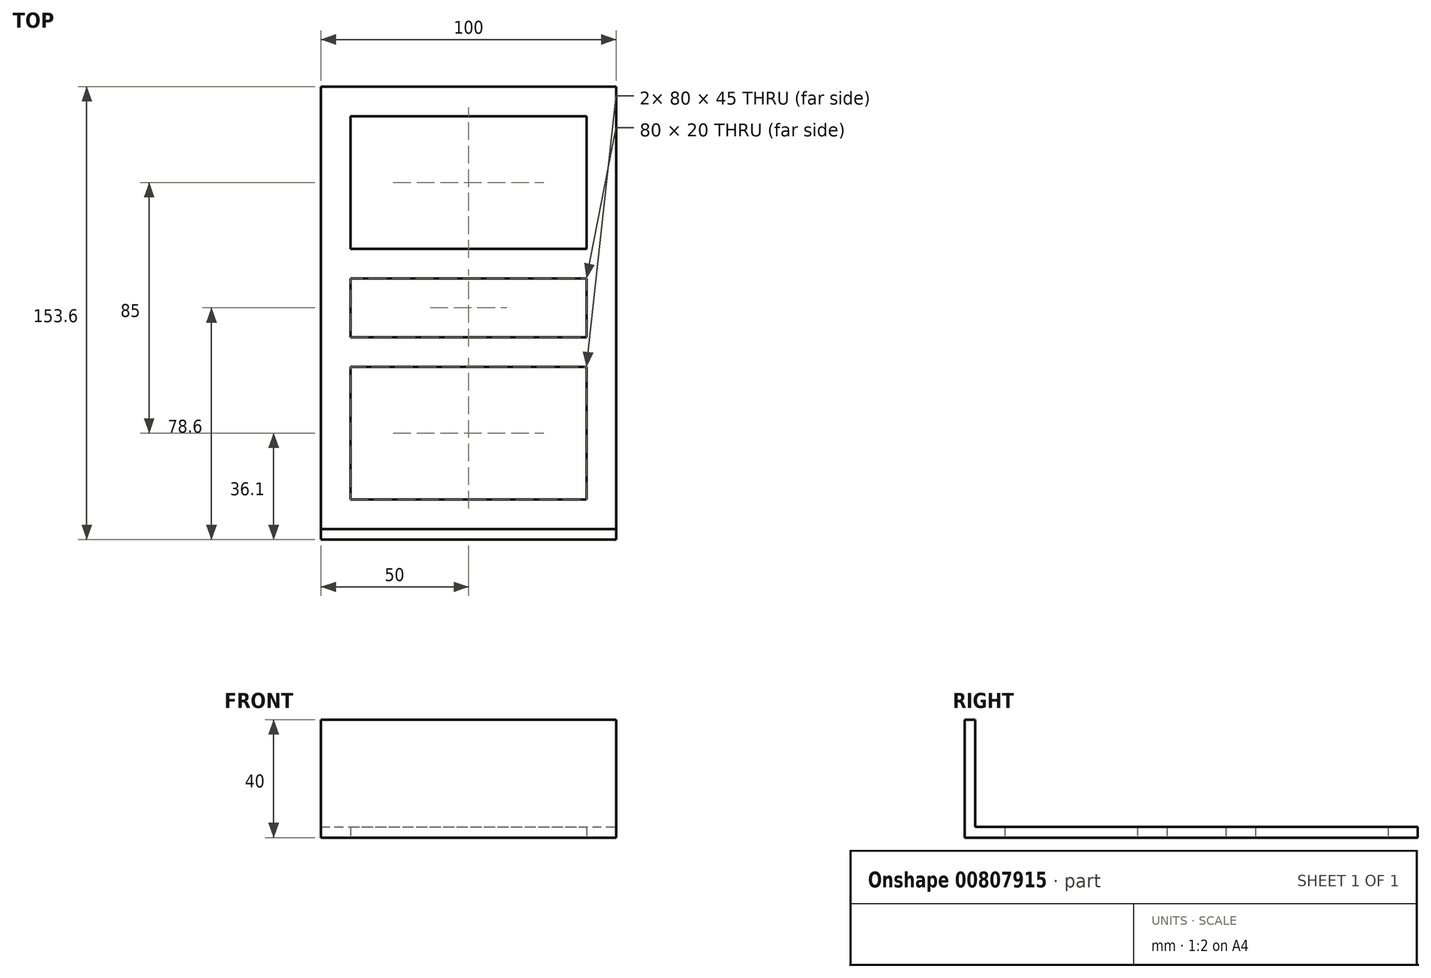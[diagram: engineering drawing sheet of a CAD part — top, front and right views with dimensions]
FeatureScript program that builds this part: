
annotation { "Feature Type Name" : "Feature", "Feature Type Description" : "" }
export const myFeature = defineFeature(function(context is Context, id is Id, definition is map)
    precondition{}
    {
        {
            var Q0;
            Q0=qCreatedBy(makeId("Top.planeOp"),FACE);
            var sketch = newSketch(context, id + "F0", { "sketchPlane" : qUnion([Q0])});
            skLineSegment(sketch, "E0.bottom", {"start": v(-50, 75) * mm, "end": v(50, 75) * mm});
            skLineSegment(sketch, "E0.top", {"start": v(-50, -75) * mm, "end": v(50, -75) * mm});
            skLineSegment(sketch, "E0.left", {"start": v(-50, 75) * mm, "end": v(-50, -75) * mm});
            skLineSegment(sketch, "E0.right", {"start": v(50, 75) * mm, "end": v(50, -75) * mm});
            skPoint(sketch, "E0.middle", {"position": v(0, 0) * mm});
            skLineSegment(sketch, "E1.bottom", {"start": v(-40, 65) * mm, "end": v(40, 65) * mm});
            skLineSegment(sketch, "E1.top", {"start": v(-40, -65) * mm, "end": v(40, -65) * mm});
            skLineSegment(sketch, "E1.left", {"start": v(-40, 65) * mm, "end": v(-40, -65) * mm});
            skLineSegment(sketch, "E1.right", {"start": v(40, 65) * mm, "end": v(40, -65) * mm});
            skLineSegment(sketch, "E2", {"start": v(-40, 20) * mm, "end": v(40, 20) * mm});
            skLineSegment(sketch, "E3", {"start": v(-40, -20) * mm, "end": v(40, -20) * mm});
            skLineSegment(sketch, "E4", {"start": v(-40, 10) * mm, "end": v(40, 10) * mm});
            skLineSegment(sketch, "E5", {"start": v(-40, -10) * mm, "end": v(40, -10) * mm});
            skSolve(sketch);
        }
        {
            var Q0;
            Q0=makeQuery(id+"F0.imprint","IMPRINT",FACE,{"disambiguationData":[TD([[makeQuery(id+"F0.imprint","IMPRINT",EDGE,{"derivedFrom":sQuery(id+"F0.wireOp",EDGE,"E0.bottom")}),-1.0]])]});
            var Q1;
            {var subQ0=sQuery(id+"F0.wireOp",EDGE,"E3");Q1=makeQuery(id+"F0.imprint","IMPRINT",FACE,{"disambiguationData":[TD([[makeQuery(id+"F0.imprint","IMPRINT",EDGE,{"derivedFrom":subQ0}),1.0]])]});}
            var Q2;
            {var subQ0=sQuery(id+"F0.wireOp",EDGE,"E2");Q2=makeQuery(id+"F0.imprint","IMPRINT",FACE,{"disambiguationData":[TD([[makeQuery(id+"F0.imprint","IMPRINT",EDGE,{"derivedFrom":subQ0}),-1.0]])]});}
            extrude(context, id + "F1", {"entities" : qUnion([Q0, Q1, Q2]), "depth" : 3.6 * mm, "offsetDistance" : 25 * mm});
        }
        {
            var Q0;
            Q0=qCreatedBy(makeId("Top.planeOp"),FACE);
            var sketch = newSketch(context, id + "F2", { "sketchPlane" : qUnion([Q0])});
            skLineSegment(sketch, "E6.bottom", {"start": v(-50, -75) * mm, "end": v(50, -75) * mm});
            skLineSegment(sketch, "E6.top", {"start": v(-50, -78.6) * mm, "end": v(50, -78.6) * mm});
            skLineSegment(sketch, "E6.left", {"start": v(-50, -75) * mm, "end": v(-50, -78.6) * mm});
            skLineSegment(sketch, "E6.right", {"start": v(50, -75) * mm, "end": v(50, -78.6) * mm});
            skPoint(sketch, "E6.middle", {"position": v(0, -76.8) * mm});
            skSolve(sketch);
        }
        {
            var Q0;
            Q0=makeQuery(id+"F2.imprint","IMPRINT",FACE,{"disambiguationData":[TD([[makeQuery(id+"F2.imprint","IMPRINT",EDGE,{"derivedFrom":sQuery(id+"F2.wireOp",EDGE,"E6.bottom")}),-1.0]])]});
            extrude(context, id + "F3", {"entities" : qUnion([Q0]), "operationType" : NewBodyOperationType.ADD, "depth" : 40 * mm, "offsetDistance" : 25 * mm});
        }
    });
